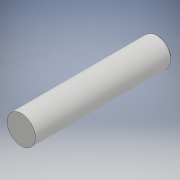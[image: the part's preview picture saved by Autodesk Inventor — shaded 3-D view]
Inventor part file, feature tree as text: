
AUTODESK INVENTOR PART (.ipt)
format: ipt  version: 2018 (Build 220112000, 112)  size: 99,328 bytes
history: native  units: mm
features: revolve x1, sketch x1
ambient origin geometry x8: Origin, YZ Plane, XZ Plane, XY Plane, X Axis, Y Axis, Z Axis, Center Point
bodies: Solid1 (feature_tree)
feature tree (2):
  revolve  "Revolution1"  [1 undecoded]
  sketch  "Sketch1"  dims[d0=67.0mm d1=1.5mm d2=45.0deg d3=14.0mm d4=90.0deg]
note: 1 required parameter value undecoded (feature->parameter linkage not recoverable at this tier; creation-order binding heuristic only, values carry confidence <= 0.55)
